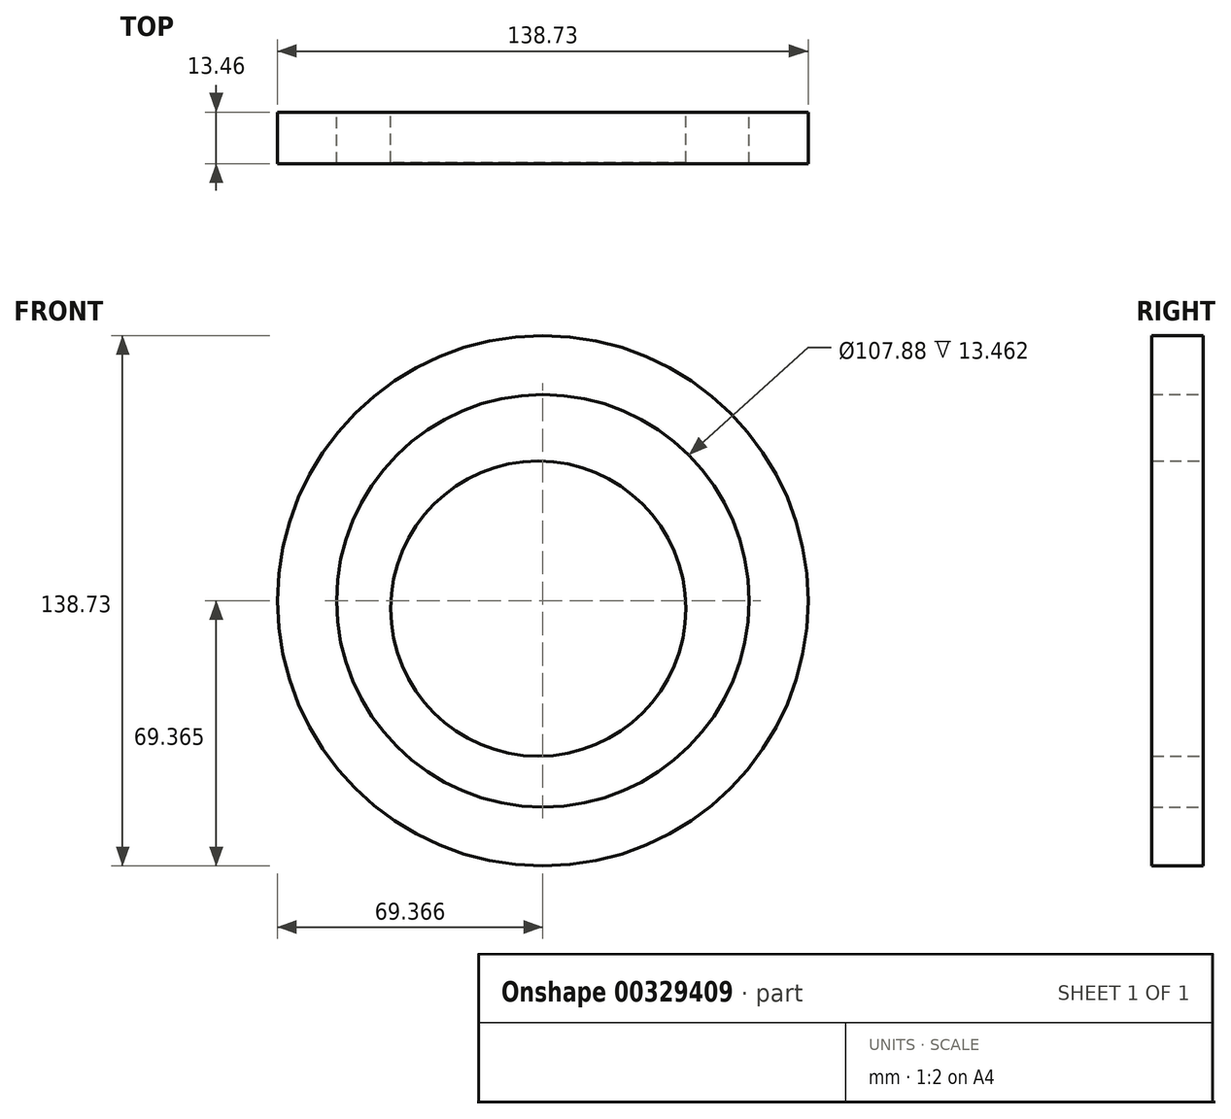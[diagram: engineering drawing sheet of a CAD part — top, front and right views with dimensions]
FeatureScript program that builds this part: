
annotation { "Feature Type Name" : "Feature", "Feature Type Description" : "" }
export const myFeature = defineFeature(function(context is Context, id is Id, definition is map)
    precondition{}
    {
        {
            var Q0;
            Q0=qCreatedBy(makeId("Front.planeOp"),FACE);
            var sketch = newSketch(context, id + "F0", { "sketchPlane" : qUnion([Q0])});
            skCircle(sketch, "E0", {"center": v(-35.72, 31.3) * mm, "radius": 69.37 * mm});
            skCircle(sketch, "E1", {"center": v(-35.72, 31.3) * mm, "radius": 53.94 * mm});
            skCircle(sketch, "E2", {"center": v(-35.72, 31.3) * mm, "radius": 37.08 * mm});
            skCircle(sketch, "E3", {"center": v(-35.72, 31.3) * mm, "radius": 24.23 * mm});
            skCircle(sketch, "E4", {"center": v(-35.72, 31.3) * mm, "radius": 13.57 * mm});
            skSolve(sketch);
        }
        {
            var Q0;
            Q0=makeQuery(id+"F0.imprint","IMPRINT",FACE,{"disambiguationData":[TD([[makeQuery(id+"F0.imprint","IMPRINT",EDGE,{"derivedFrom":sQuery(id+"F0.wireOp",EDGE,"E0")}),1.0]])]});
            extrude(context, id + "F1", {"entities" : qUnion([Q0]), "depth" : 13.46 * mm});
        }
        {
            var Q0;
            Q0=qCreatedBy(makeId("Front.planeOp"),FACE);
            var sketch = newSketch(context, id + "F2", { "sketchPlane" : qUnion([Q0])});
            skCircle(sketch, "E5", {"center": v(-36.91, 29.25) * mm, "radius": 38.6 * mm});
            skSolve(sketch);
        }
        {
            var Q0;
            Q0=makeQuery(id+"F2.imprint","IMPRINT",FACE,{"disambiguationData":[TD([[makeQuery(id+"F2.imprint","IMPRINT",EDGE,{"derivedFrom":sQuery(id+"F2.wireOp",EDGE,"E5")}),1.0]])]});
            extrude(context, id + "F3", {"entities" : qUnion([Q0]), "depth" : 13.2 * mm});
        }
    });
